# Revit family: Water_Heaters_HAJDU_HAJDU-Z-S-ErP_
name_source: partatom
category: Mechanical Equipment
units: mm (PartAtom-declared; Revit-internal decimal feet)

## family parameters
Always vertical = Yes
Classification = None
Cut with Voids When Loaded = No
Maintain Annotation Orientation = No
OmniClass Number = 23.31.29.13
OmniClass Title = Hot Water Tank Heaters
Part Type = Normal
Room Calculation Point = No
Round Connector Dimension = Use Diameter
Shared = No
Work Plane-Based = Yes

## types (1)
- Nem típus - Terheléstípus katalógus!
    A melegvíz maximális homérséklete = 75 °C
    Case Material = Hajdu - Felület - Fehér
    Csapolási profil = L
    Csatlakozás leírása = Elektromos csatlakozó
    Csatlakozó magassága "A" = 231 mm  [stored 0.757874 ft]
    Csatlakozó magassága "B" = 510 mm  [stored 1.67323 ft]
    Csatlakozó magassága "C" = 317 mm  [stored 1.04003 ft]
    Default Elevation = 1219.2 mm  [stored 4 ft]
    Description = Az elektromos, zártrendszerű forróvíztárolók a használati melegvíz igény kielégítésére szolgálnak. A zártrendszerű tárolós vízmelegítők tartálya acéllemezből készül, a korrózió elleni védelmet speciális, titán tartalmú tűzzománc bevonat és aktív magnézium anód biztosítja. Ezek a készülékek több vízvételi hely, illetve zuhanyzós csaptelepek ellátására alkalmasak. A készülékek hőszigetelése freonmentes, poliuretán szigetelő hab. A fémburkolatú kivitelek nanokerámiás felület előkészítéssel rendelkeznek. Űrtartalom: 150, 200, 300 liter.Kivezetett hőfokszabályzó.Elhelyezési lehetőség: álló. (A gépkönyvben így szerepel: „padlón álló”.)
    Energiahatékonysági osztály = C
    Felfutési ido 15°C-ról 65°C-ra = 4 h
    Feszültség = 230 V
    Frekvencia = 50 Hz
    Futobetét típusa = csőfűtőtest
    Futoteljesítmény = 2400 W
    Fázisok száma = 1
    Látszólagos terhelés = 2530 VA
    Magasság = 1035 mm  [stored 3.39567 ft]
    Manufacturer = HAJDU
    Model = Modell nincs megadva - Terheléstípus katalógus!
    Mélység = 669 mm  [stored 2.19488 ft]
    Névleges urtartalom = 150 l
    Névleges üzemi nyomás = 0.6 MPa
    Product Page URL = https://hajdurt.hu
    Rádiusz = 297.5 mm  [stored 0.97605 ft]
    Teljesítménytényezo = 1
    Tömeg = 50.00 kg
    URL = https://hajdurt.hu
    Vízcsatlakozás = 19.05 mm  [stored 0.0625 ft]
    Áramfelvétel = 11 A
    Átméro = 595 mm  [stored 1.9521 ft]

note: [stored X ft] marks values corroborated as IEEE doubles in the binary element streams (Revit-internal decimal feet)

## geometry (parser evidence)
native form markers: Sweep x5
no freeform markers — native parametric forms only
